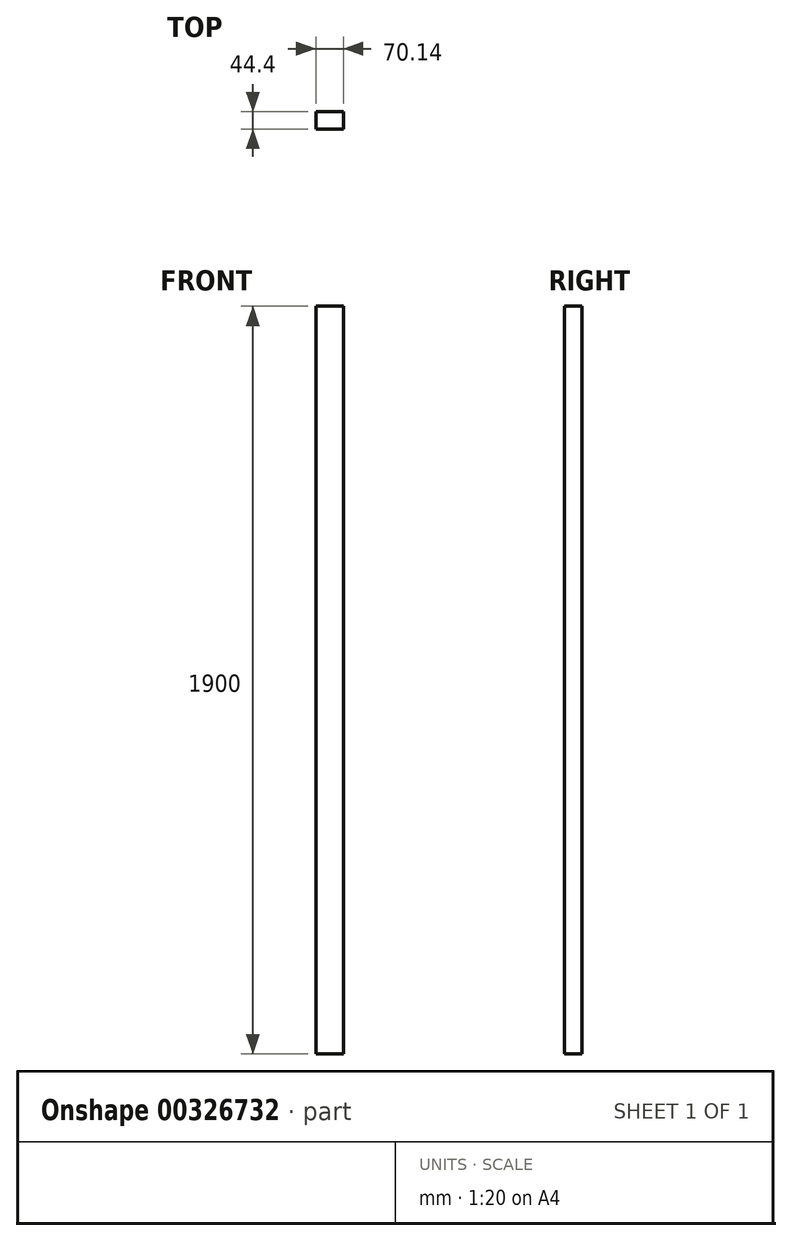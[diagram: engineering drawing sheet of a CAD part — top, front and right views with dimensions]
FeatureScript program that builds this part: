
annotation { "Feature Type Name" : "Feature", "Feature Type Description" : "" }
export const myFeature = defineFeature(function(context is Context, id is Id, definition is map)
    precondition{}
    {
        {
            var Q0;
            Q0=qCreatedBy(makeId("Top.planeOp"),FACE);
            var sketch = newSketch(context, id + "F0", { "sketchPlane" : qUnion([Q0])});
            skLineSegment(sketch, "E0.bottom", {"start": v(35.07, -22.2) * mm, "end": v(-35.07, -22.2) * mm});
            skLineSegment(sketch, "E0.top", {"start": v(35.07, 22.2) * mm, "end": v(-35.07, 22.2) * mm});
            skLineSegment(sketch, "E0.left", {"start": v(35.07, -22.2) * mm, "end": v(35.07, 22.2) * mm});
            skLineSegment(sketch, "E0.right", {"start": v(-35.07, -22.2) * mm, "end": v(-35.07, 22.2) * mm});
            skPoint(sketch, "E0.middle", {"position": v(0, 0) * mm});
            skSolve(sketch);
        }
        {
            var Q0;
            Q0=makeQuery(id+"F0.imprint","IMPRINT",FACE,{"disambiguationData":[TD([[makeQuery(id+"F0.imprint","IMPRINT",EDGE,{"derivedFrom":sQuery(id+"F0.wireOp",EDGE,"E0.bottom")}),-1.0]])]});
            extrude(context, id + "F1", {"entities" : qUnion([Q0]), "depth" : 1900 * mm, "offsetDistance" : 25 * mm});
        }
    });
